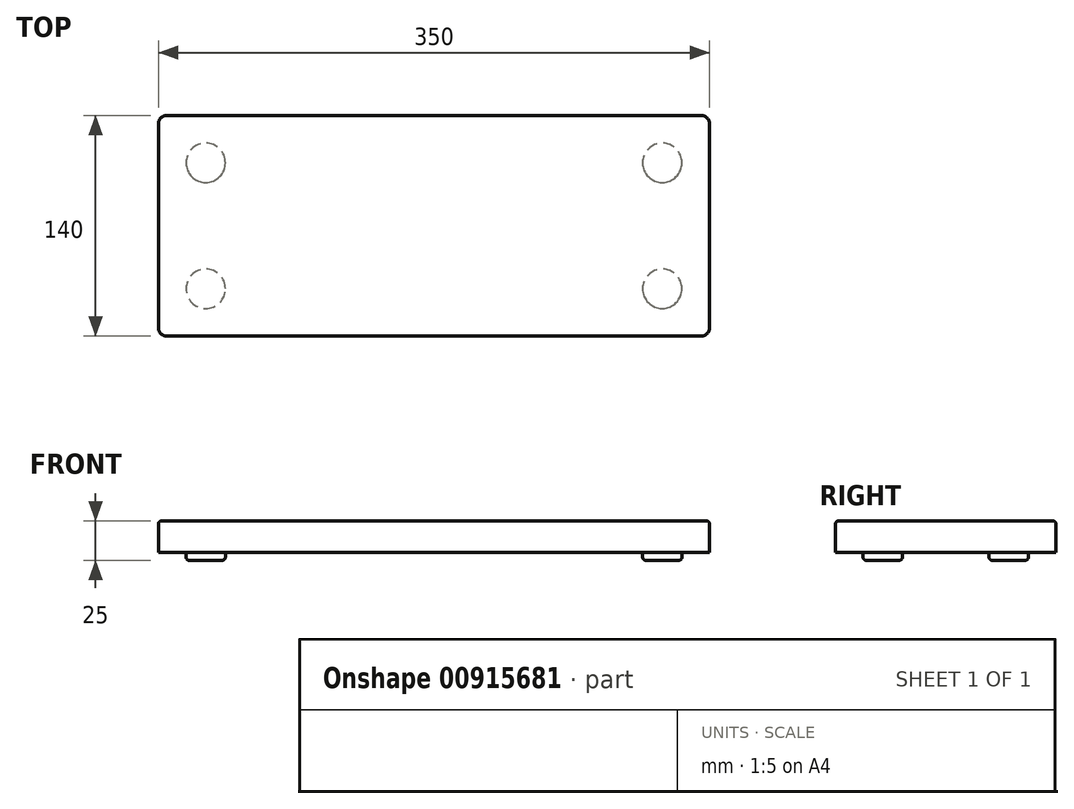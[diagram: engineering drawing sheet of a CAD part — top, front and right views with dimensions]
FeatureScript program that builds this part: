
annotation { "Feature Type Name" : "Feature", "Feature Type Description" : "" }
export const myFeature = defineFeature(function(context is Context, id is Id, definition is map)
    precondition{}
    {
        {
            var Q0;
            Q0=qCreatedBy(makeId("Top.planeOp"),FACE);
            var sketch = newSketch(context, id + "F0", { "sketchPlane" : qUnion([Q0])});
            skLineSegment(sketch, "E0.bottom", {"start": v(175, -70) * mm, "end": v(-175, -70) * mm});
            skLineSegment(sketch, "E0.top", {"start": v(175, 70) * mm, "end": v(-175, 70) * mm});
            skLineSegment(sketch, "E0.left", {"start": v(175, -70) * mm, "end": v(175, 70) * mm});
            skLineSegment(sketch, "E0.right", {"start": v(-175, -70) * mm, "end": v(-175, 70) * mm});
            skPoint(sketch, "E0.middle", {"position": v(0, 0) * mm});
            skSolve(sketch);
        }
        {
            var Q0;
            Q0=makeQuery(id+"F0.imprint","IMPRINT",FACE,{"disambiguationData":[TD([[makeQuery(id+"F0.imprint","IMPRINT",EDGE,{"derivedFrom":sQuery(id+"F0.wireOp",EDGE,"E0.bottom")}),-1.0]])]});
            extrude(context, id + "F1", {"entities" : qUnion([Q0]), "depth" : 20 * mm, "offsetDistance" : 25 * mm});
        }
        {
            var Q0;
            Q0=makeQuery(id+"F1.opExtrude","CAP_FACE",FACE,{"disambiguationData":[OSD([sQuery(id+"F0.wireOp",EDGE,"E0.bottom"),sQuery(id+"F0.wireOp",EDGE,"E0.top"),sQuery(id+"F0.wireOp",EDGE,"E0.left"),sQuery(id+"F0.wireOp",EDGE,"E0.right")])],"isStart":true});
            var sketch = newSketch(context, id + "F2", { "sketchPlane" : qUnion([Q0])});
            skPoint(sketch, "E1", {"position": v(-145, 40) * mm});
            skPoint(sketch, "E2", {"position": v(-295.8, -95.6) * mm});
            skPoint(sketch, "E3", {"position": v(297.28, -100.71) * mm});
            skPoint(sketch, "E4", {"position": v(289.62, 106.64) * mm});
            skPoint(sketch, "E5", {"position": v(-145, -40) * mm});
            skPoint(sketch, "E6", {"position": v(145, -40) * mm});
            skPoint(sketch, "E7", {"position": v(145, 40) * mm});
            skCircle(sketch, "E8", {"center": v(-145, 40) * mm, "radius": 12.5 * mm});
            skCircle(sketch, "E9", {"center": v(-145, -40) * mm, "radius": 12.5 * mm});
            skCircle(sketch, "E10", {"center": v(145, -40) * mm, "radius": 12.5 * mm});
            skCircle(sketch, "E11", {"center": v(145, 40) * mm, "radius": 12.5 * mm});
            skSolve(sketch);
        }
        {
            var Q0;
            Q0=makeQuery(id+"F2.imprint","IMPRINT",FACE,{"disambiguationData":[TD([[makeQuery(id+"F2.imprint","IMPRINT",EDGE,{"derivedFrom":sQuery(id+"F2.wireOp",EDGE,"E11")}),1.0]])]});
            var Q1;
            Q1=makeQuery(id+"F2.imprint","IMPRINT",FACE,{"disambiguationData":[TD([[makeQuery(id+"F2.imprint","IMPRINT",EDGE,{"derivedFrom":sQuery(id+"F2.wireOp",EDGE,"E10")}),1.0]])]});
            var Q2;
            Q2=makeQuery(id+"F2.imprint","IMPRINT",FACE,{"disambiguationData":[TD([[makeQuery(id+"F2.imprint","IMPRINT",EDGE,{"derivedFrom":sQuery(id+"F2.wireOp",EDGE,"E8")}),1.0]])]});
            var Q3;
            Q3=makeQuery(id+"F2.imprint","IMPRINT",FACE,{"disambiguationData":[TD([[makeQuery(id+"F2.imprint","IMPRINT",EDGE,{"derivedFrom":sQuery(id+"F2.wireOp",EDGE,"E9")}),1.0]])]});
            extrude(context, id + "F3", {"entities" : qUnion([Q0, Q1, Q2, Q3]), "operationType" : NewBodyOperationType.ADD, "depth" : 5 * mm, "offsetDistance" : 25 * mm});
        }
        {
            var Q0;
            Q0=makeQuery(id+"F3.opExtrude","CAP_EDGE",EDGE,{"disambiguationData":[OSD([sQuery(id+"F2.wireOp",EDGE,"E8")])],"isStart":false});
            var Q1;
            Q1=makeQuery(id+"F3.opExtrude","CAP_EDGE",EDGE,{"disambiguationData":[OSD([sQuery(id+"F2.wireOp",EDGE,"E9")])],"isStart":false});
            var Q2;
            Q2=makeQuery(id+"F3.opExtrude","CAP_EDGE",EDGE,{"disambiguationData":[OSD([sQuery(id+"F2.wireOp",EDGE,"E10")])],"isStart":false});
            var Q3;
            Q3=makeQuery(id+"F3.opExtrude","CAP_EDGE",EDGE,{"disambiguationData":[OSD([sQuery(id+"F2.wireOp",EDGE,"E11")])],"isStart":false});
            fillet(context, id + "F4", {"entities" : qUnion([Q0, Q1, Q2, Q3]), "radius" : 2 * mm, "tangentPropagation" : true, "allowEdgeOverflow" : false});
        }
        {
            var Q0;
            Q0=makeQuery(id+"F1.opExtrude","SWEPT_EDGE",EDGE,{"disambiguationData":[OSD([sQuery(id+"F0.wireOp",EDGE,"E0.bottom"),sQuery(id+"F0.wireOp",EDGE,"E0.right")])]});
            var Q1;
            Q1=makeQuery(id+"F1.opExtrude","SWEPT_EDGE",EDGE,{"disambiguationData":[OSD([sQuery(id+"F0.wireOp",EDGE,"E0.top"),sQuery(id+"F0.wireOp",EDGE,"E0.right")])]});
            var Q2;
            Q2=makeQuery(id+"F1.opExtrude","SWEPT_EDGE",EDGE,{"disambiguationData":[OSD([sQuery(id+"F0.wireOp",EDGE,"E0.bottom"),sQuery(id+"F0.wireOp",EDGE,"E0.left")])]});
            var Q3;
            Q3=makeQuery(id+"F1.opExtrude","SWEPT_EDGE",EDGE,{"disambiguationData":[OSD([sQuery(id+"F0.wireOp",EDGE,"E0.top"),sQuery(id+"F0.wireOp",EDGE,"E0.left")])]});
            fillet(context, id + "F5", {"entities" : qUnion([Q0, Q1, Q2, Q3]), "radius" : 5 * mm, "tangentPropagation" : true, "allowEdgeOverflow" : false});
        }
        {
            var Q0;
            Q0=makeQuery(id+"F1.opExtrude","CAP_EDGE",EDGE,{"disambiguationData":[OSD([sQuery(id+"F0.wireOp",EDGE,"E0.left")])],"isStart":false});
            fillet(context, id + "F6", {"entities" : qUnion([Q0]), "radius" : 2 * mm, "tangentPropagation" : true, "allowEdgeOverflow" : false});
        }
    });
